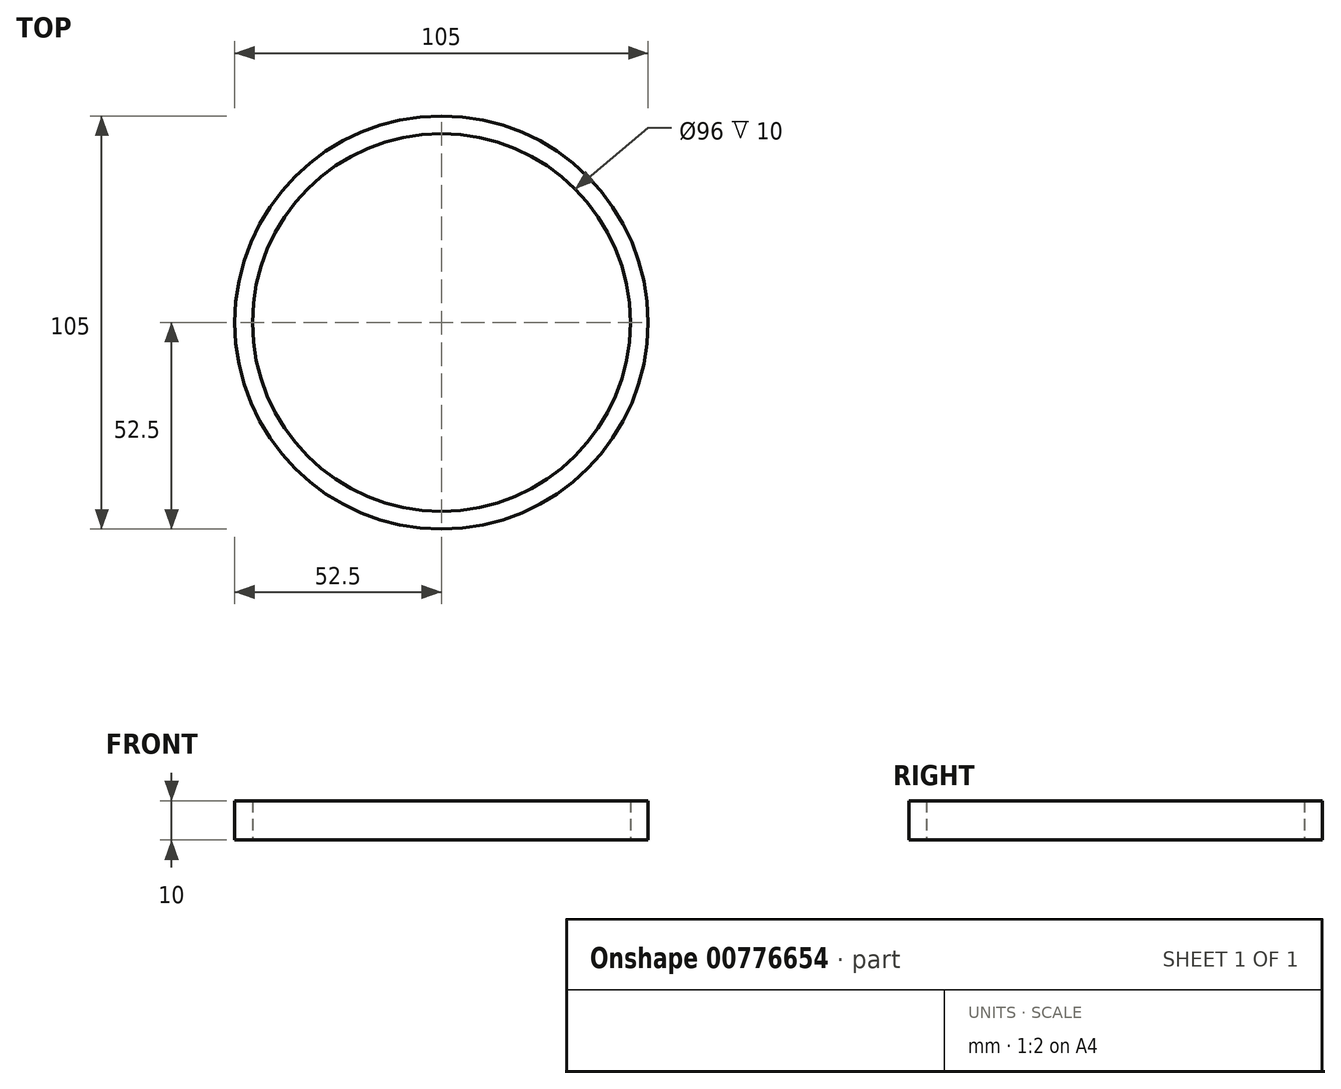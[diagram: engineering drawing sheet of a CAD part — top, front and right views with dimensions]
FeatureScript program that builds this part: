
annotation { "Feature Type Name" : "Feature", "Feature Type Description" : "" }
export const myFeature = defineFeature(function(context is Context, id is Id, definition is map)
    precondition{}
    {
        {
            var Q0;
            Q0=qCreatedBy(makeId("Top.planeOp"),FACE);
            var sketch = newSketch(context, id + "F0", { "sketchPlane" : qUnion([Q0])});
            skCircle(sketch, "E0", {"center": v(0, 0) * mm, "radius": 48 * mm});
            skCircle(sketch, "E1", {"center": v(0, 0) * mm, "radius": 52.5 * mm});
            skSolve(sketch);
        }
        {
            var Q0;
            Q0=makeQuery(id+"F0.imprint","IMPRINT",FACE,{"disambiguationData":[TD([[makeQuery(id+"F0.imprint","IMPRINT",EDGE,{"derivedFrom":sQuery(id+"F0.wireOp",EDGE,"E0")}),-1.0]])]});
            extrude(context, id + "F1", {"entities" : qUnion([Q0]), "depth" : 10 * mm, "offsetDistance" : 25 * mm});
        }
    });
